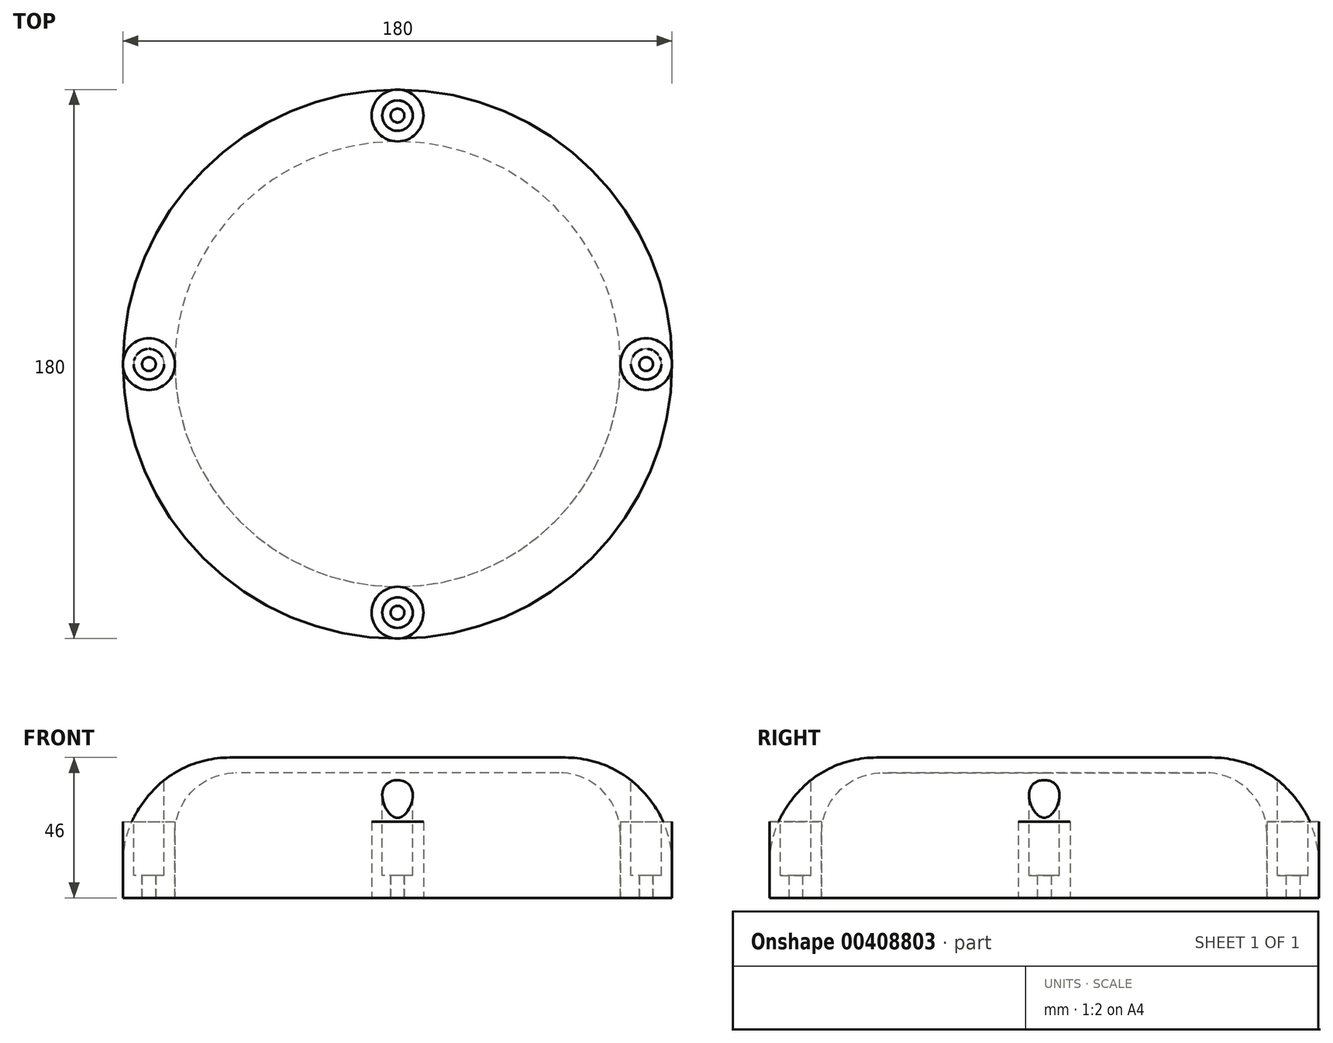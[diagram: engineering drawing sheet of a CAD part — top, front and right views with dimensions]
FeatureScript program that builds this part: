
annotation { "Feature Type Name" : "Feature", "Feature Type Description" : "" }
export const myFeature = defineFeature(function(context is Context, id is Id, definition is map)
    precondition{}
    {
        {
            var Q0;
            Q0=qCreatedBy(makeId("Top.planeOp"),FACE);
            var sketch = newSketch(context, id + "F0", { "sketchPlane" : qUnion([Q0])});
            skCircle(sketch, "E0", {"center": v(0, 0) * mm, "radius": 58 * mm});
            skCircle(sketch, "E1", {"center": v(0, 0) * mm, "radius": 61 * mm});
            skSolve(sketch);
        }
        {
            var Q0;
            Q0=makeQuery(id+"F0.imprint","IMPRINT",FACE,{"disambiguationData":[TD([[makeQuery(id+"F0.imprint","IMPRINT",EDGE,{"derivedFrom":sQuery(id+"F0.wireOp",EDGE,"E0")}),-1.0]])]});
            extrude(context, id + "F1", {"entities" : qUnion([Q0]), "depth" : 4 * mm});
        }
        {
            var Q0;
            Q0=qCreatedBy(makeId("Top.planeOp"),FACE);
            var sketch = newSketch(context, id + "F2", { "sketchPlane" : qUnion([Q0])});
            skCircle(sketch, "E2.0", {"center": v(0, 0) * mm, "radius": 56 * mm});
            skCircle(sketch, "E3.0", {"center": v(0, 0) * mm, "radius": 61 * mm});
            skSolve(sketch);
        }
        {
            var Q0;
            Q0=makeQuery(id+"F2.imprint","IMPRINT",FACE,{"disambiguationData":[TD([[makeQuery(id+"F2.imprint","IMPRINT",EDGE,{"derivedFrom":sQuery(id+"F2.wireOp",EDGE,"E2.0")}),-1.0]])]});
            extrude(context, id + "F3", {"entities" : qUnion([Q0]), "operationType" : NewBodyOperationType.ADD, "oppositeDirection" : true, "depth" : 3 * mm});
        }
        {
            var Q0;
            Q0=makeQuery(id+"F3.opExtrude","CAP_EDGE",EDGE,{"disambiguationData":[OSD([sQuery(id+"F2.wireOp",EDGE,"E2.0")])],"isStart":true});
            chamfer(context, id + "F4", {"entities" : qUnion([Q0]), "width" : 2 * mm, "tangentPropagation" : true});
        }
        {
            var Q0;
            Q0=makeQuery(id+"F3.opExtrude","CAP_FACE",FACE,{"disambiguationData":[OSD([sQuery(id+"F2.wireOp",EDGE,"E2.0"),sQuery(id+"F2.wireOp",EDGE,"E3.0")])],"isStart":false});
            var sketch = newSketch(context, id + "F5", { "sketchPlane" : qUnion([Q0])});
            skCircle(sketch, "E4", {"center": v(-46.45, 46.18) * mm, "radius": 7.5 * mm});
            skLineSegment(sketch, "E5", {"start": v(-53.95, 46.18) * mm, "end": v(-53.95, 28.46) * mm});
            skCircle(sketch, "E6", {"center": v(-46.45, 46.18) * mm, "radius": 2.25 * mm});
            skLineSegment(sketch, "E7", {"start": v(-46.57, 53.68) * mm, "end": v(-28.43, 53.97) * mm});
            skLineSegment(sketch, "E8.1.0", {"start": v(-53.68, -46.57) * mm, "end": v(-53.97, -28.43) * mm});
            skCircle(sketch, "E8.1.1", {"center": v(-46.18, -46.45) * mm, "radius": 7.5 * mm});
            skCircle(sketch, "E8.1.2", {"center": v(-46.18, -46.45) * mm, "radius": 2.25 * mm});
            skLineSegment(sketch, "E8.1.3", {"start": v(-46.18, -53.95) * mm, "end": v(-28.46, -53.95) * mm});
            skLineSegment(sketch, "E8.2.0", {"start": v(46.57, -53.68) * mm, "end": v(28.43, -53.97) * mm});
            skCircle(sketch, "E8.2.1", {"center": v(46.45, -46.18) * mm, "radius": 7.5 * mm});
            skCircle(sketch, "E8.2.2", {"center": v(46.45, -46.18) * mm, "radius": 2.25 * mm});
            skLineSegment(sketch, "E8.2.3", {"start": v(53.95, -46.18) * mm, "end": v(53.95, -28.46) * mm});
            skLineSegment(sketch, "E8.3.0", {"start": v(53.68, 46.57) * mm, "end": v(53.97, 28.43) * mm});
            skCircle(sketch, "E8.3.1", {"center": v(46.18, 46.45) * mm, "radius": 7.5 * mm});
            skCircle(sketch, "E8.3.2", {"center": v(46.18, 46.45) * mm, "radius": 2.25 * mm});
            skLineSegment(sketch, "E8.3.3", {"start": v(46.18, 53.95) * mm, "end": v(28.46, 53.95) * mm});
            skPoint(sketch, "E8.center", {"position": v(0, 0) * mm});
            skSolve(sketch);
        }
        {
            var Q0;
            Q0=qSketchRegion(id+"F5",true);
            var Q1;
            {var subQ0=sQuery(id+"F5.wireOp",EDGE,"E5");Q1=makeQuery(id+"F5.imprint","IMPRINT",FACE,{"disambiguationData":[TD([[makeQuery(id+"F5.imprint","IMPRINT",EDGE,{"derivedFrom":subQ0}),1.0]])]});}
            var Q2;
            {var subQ0=sQuery(id+"F5.wireOp",EDGE,"E7");Q2=makeQuery(id+"F5.imprint","IMPRINT",FACE,{"disambiguationData":[TD([[makeQuery(id+"F5.imprint","IMPRINT",EDGE,{"derivedFrom":subQ0}),-1.0]])]});}
            var Q3;
            {var subQ0=sQuery(id+"F5.wireOp",EDGE,"E8.3.3");Q3=makeQuery(id+"F5.imprint","IMPRINT",FACE,{"disambiguationData":[TD([[makeQuery(id+"F5.imprint","IMPRINT",EDGE,{"derivedFrom":subQ0}),1.0]])]});}
            var Q4;
            {var subQ0=sQuery(id+"F5.wireOp",EDGE,"E8.3.0");Q4=makeQuery(id+"F5.imprint","IMPRINT",FACE,{"disambiguationData":[TD([[makeQuery(id+"F5.imprint","IMPRINT",EDGE,{"derivedFrom":subQ0}),-1.0]])]});}
            var Q5;
            {var subQ0=sQuery(id+"F5.wireOp",EDGE,"E8.2.3");Q5=makeQuery(id+"F5.imprint","IMPRINT",FACE,{"disambiguationData":[TD([[makeQuery(id+"F5.imprint","IMPRINT",EDGE,{"derivedFrom":subQ0}),1.0]])]});}
            var Q6;
            {var subQ0=sQuery(id+"F5.wireOp",EDGE,"E8.2.0");Q6=makeQuery(id+"F5.imprint","IMPRINT",FACE,{"disambiguationData":[TD([[makeQuery(id+"F5.imprint","IMPRINT",EDGE,{"derivedFrom":subQ0}),-1.0]])]});}
            var Q7;
            {var subQ0=sQuery(id+"F5.wireOp",EDGE,"E8.1.3");Q7=makeQuery(id+"F5.imprint","IMPRINT",FACE,{"disambiguationData":[TD([[makeQuery(id+"F5.imprint","IMPRINT",EDGE,{"derivedFrom":subQ0}),1.0]])]});}
            var Q8;
            {var subQ0=sQuery(id+"F5.wireOp",EDGE,"E8.1.0");Q8=makeQuery(id+"F5.imprint","IMPRINT",FACE,{"disambiguationData":[TD([[makeQuery(id+"F5.imprint","IMPRINT",EDGE,{"derivedFrom":subQ0}),-1.0]])]});}
            extrude(context, id + "F6", {"entities" : qUnion([Q0, Q1, Q2, Q3, Q4, Q5, Q6, Q7, Q8]), "operationType" : NewBodyOperationType.ADD, "oppositeDirection" : true, "depth" : 7 * mm});
        }
        {
            var Q0;
            Q0=makeQuery(id+"F6.opExtrude","CAP_EDGE",EDGE,{"disambiguationData":[OSD([sQuery(id+"F5.wireOp",EDGE,"E8.3.2")])],"isStart":true});
            var Q1;
            Q1=makeQuery(id+"F6.opExtrude","CAP_EDGE",EDGE,{"disambiguationData":[OSD([sQuery(id+"F5.wireOp",EDGE,"E8.2.2")])],"isStart":true});
            var Q2;
            Q2=makeQuery(id+"F6.opExtrude","CAP_EDGE",EDGE,{"disambiguationData":[OSD([sQuery(id+"F5.wireOp",EDGE,"E8.1.2")])],"isStart":true});
            var Q3;
            Q3=makeQuery(id+"F6.opExtrude","CAP_EDGE",EDGE,{"disambiguationData":[OSD([sQuery(id+"F5.wireOp",EDGE,"E6")])],"isStart":true});
            chamfer(context, id + "F7", {"entities" : qUnion([Q0, Q1, Q2, Q3]), "width" : 3 * mm, "tangentPropagation" : true});
        }
        {
            var Q0;
            {var subQ0=sQuery(id+"F2.wireOp",EDGE,"E3.0");Q0=makeQuery(id+"F6.boolean.opBoolean","MERGE",FACE,{"derivedFrom":[makeQuery(id+"F1.opExtrude","CAP_FACE",FACE,{"disambiguationData":[OSD([sQuery(id+"F0.wireOp",EDGE,"E0"),sQuery(id+"F0.wireOp",EDGE,"E1")])],"isStart":false}),makeQuery(id+"F6.opExtrude","CAP_FACE",FACE,{"disambiguationData":[OSD([subQ0,sQuery(id+"F5.wireOp",EDGE,"E4"),sQuery(id+"F5.wireOp",EDGE,"E5"),sQuery(id+"F5.wireOp",EDGE,"E6"),sQuery(id+"F5.wireOp",EDGE,"E7")])],"isStart":false}),makeQuery(id+"F6.opExtrude","CAP_FACE",FACE,{"disambiguationData":[OSD([subQ0,sQuery(id+"F5.wireOp",EDGE,"E8.1.0"),sQuery(id+"F5.wireOp",EDGE,"E8.1.1"),sQuery(id+"F5.wireOp",EDGE,"E8.1.2"),sQuery(id+"F5.wireOp",EDGE,"E8.1.3")])],"isStart":false}),makeQuery(id+"F6.opExtrude","CAP_FACE",FACE,{"disambiguationData":[OSD([subQ0,sQuery(id+"F5.wireOp",EDGE,"E8.2.0"),sQuery(id+"F5.wireOp",EDGE,"E8.2.1"),sQuery(id+"F5.wireOp",EDGE,"E8.2.2"),sQuery(id+"F5.wireOp",EDGE,"E8.2.3")])],"isStart":false}),makeQuery(id+"F6.opExtrude","CAP_FACE",FACE,{"disambiguationData":[OSD([subQ0,sQuery(id+"F5.wireOp",EDGE,"E8.3.0"),sQuery(id+"F5.wireOp",EDGE,"E8.3.1"),sQuery(id+"F5.wireOp",EDGE,"E8.3.2"),sQuery(id+"F5.wireOp",EDGE,"E8.3.3")])],"isStart":false})]});}
            var sketch = newSketch(context, id + "F8", { "sketchPlane" : qUnion([Q0])});
            skCircle(sketch, "E9.0", {"center": v(0, 0) * mm, "radius": 56 * mm});
            skCircle(sketch, "E10.0", {"center": v(0, 0) * mm, "radius": 76 * mm});
            skCircle(sketch, "E11", {"center": v(-46.18, 46.45) * mm, "radius": 2.25 * mm});
            skCircle(sketch, "E12", {"center": v(46.45, 46.18) * mm, "radius": 2.25 * mm});
            skCircle(sketch, "E13", {"center": v(46.18, -46.45) * mm, "radius": 2.25 * mm});
            skCircle(sketch, "E14", {"center": v(-46.45, -46.18) * mm, "radius": 2.25 * mm});
            skSolve(sketch);
        }
        {
            var Q0;
            Q0=makeQuery(id+"F8.imprint","IMPRINT",FACE,{"disambiguationData":[TD([[makeQuery(id+"F8.imprint","IMPRINT",EDGE,{"derivedFrom":sQuery(id+"F8.wireOp",EDGE,"E10.0")}),1.0]])]});
            var Q1;
            Q1=makeQuery(id+"F8.imprint","IMPRINT",FACE,{"disambiguationData":[TD([[makeQuery(id+"F8.imprint","IMPRINT",EDGE,{"derivedFrom":sQuery(id+"F8.wireOp",EDGE,"E11")}),1.0]])]});
            extrude(context, id + "F9", {"entities" : qUnion([Q0, Q1]), "operationType" : NewBodyOperationType.ADD, "depth" : 4 * mm});
        }
        {
            var Q0;
            Q0=qCreatedBy(makeId("Right.planeOp"),FACE);
            var sketch = newSketch(context, id + "F10", { "sketchPlane" : qUnion([Q0])});
            skLineSegment(sketch, "E15", {"start": v(89.8, 0) * mm, "end": v(-100.67, 0) * mm});
            skLineSegment(sketch, "E16.0", {"start": v(89.8, 4) * mm, "end": v(-100.67, 4) * mm});
            skLineSegment(sketch, "E17.0", {"start": v(89.8, -3) * mm, "end": v(-100.67, -3) * mm});
            skLineSegment(sketch, "E18", {"start": v(89.8, 4) * mm, "end": v(89.8, -3) * mm});
            skLineSegment(sketch, "E19", {"start": v(-100.67, 4) * mm, "end": v(-100.67, -3) * mm});
            skSolve(sketch);
        }
        {
            var Q0;
            {var subQ0=sQuery(id+"F10.wireOp",EDGE,"E15");Q0=makeQuery(id+"F10.imprint","IMPRINT",FACE,{"disambiguationData":[TD([[makeQuery(id+"F10.imprint","IMPRINT",EDGE,{"derivedFrom":subQ0}),1.0]])]});}
            var Q1;
            {var subQ0=sQuery(id+"F10.wireOp",EDGE,"E15");Q1=makeQuery(id+"F10.imprint","IMPRINT",FACE,{"disambiguationData":[TD([[makeQuery(id+"F10.imprint","IMPRINT",EDGE,{"derivedFrom":subQ0}),-1.0]])]});}
            extrude(context, id + "F11", {"entities" : qUnion([Q0, Q1]), "operationType" : NewBodyOperationType.REMOVE, "endBound" : BoundingType.SYMMETRIC, "depth" : 200 * mm});
        }
        {
            var Q0;
            Q0=makeQuery(id+"F11.boolean.opBoolean","MERGE",FACE,{"derivedFrom":[makeQuery(id+"F9.opExtrude","CAP_FACE",FACE,{"disambiguationData":[OSD([sQuery(id+"F0.wireOp",EDGE,"E0"),sQuery(id+"F8.wireOp",EDGE,"E10.0"),sQuery(id+"F8.wireOp",EDGE,"E11"),sQuery(id+"F8.wireOp",EDGE,"E12"),sQuery(id+"F8.wireOp",EDGE,"E13"),sQuery(id+"F8.wireOp",EDGE,"E14")])],"isStart":true}),makeQuery(id+"F11.opExtrude","SWEPT_FACE",FACE,{"disambiguationData":[OSD([sQuery(id+"F10.wireOp",EDGE,"E16.0")])]})]});
            var sketch = newSketch(context, id + "F12", { "sketchPlane" : qUnion([Q0])});
            skCircle(sketch, "E20.0", {"center": v(0, 0) * mm, "radius": 73 * mm});
            skCircle(sketch, "E21.0", {"center": v(0, 0) * mm, "radius": 90 * mm});
            skCircle(sketch, "E22", {"center": v(0, 81.5) * mm, "radius": 8.5 * mm});
            skCircle(sketch, "E23", {"center": v(0, 81.5) * mm, "radius": 2.25 * mm});
            skCircle(sketch, "E24.1.0", {"center": v(-81.5, 0) * mm, "radius": 2.25 * mm});
            skCircle(sketch, "E24.1.1", {"center": v(-81.5, 0) * mm, "radius": 8.5 * mm});
            skCircle(sketch, "E24.2.0", {"center": v(0, -81.5) * mm, "radius": 2.25 * mm});
            skCircle(sketch, "E24.2.1", {"center": v(0, -81.5) * mm, "radius": 8.5 * mm});
            skCircle(sketch, "E24.3.0", {"center": v(81.5, 0) * mm, "radius": 2.25 * mm});
            skCircle(sketch, "E24.3.1", {"center": v(81.5, 0) * mm, "radius": 8.5 * mm});
            skSolve(sketch);
        }
        {
            var Q0;
            Q0 = qSketchRegion(id + "F12", true);
            var Q1;
            Q1 = qSketchRegion(id + "F14", true);
            extrude(context, id + "F13", {"entities" : qUnion([Q0, Q1]), "operationType" : NewBodyOperationType.ADD, "depth" : 50 * mm});
        }
        {
            var Q0;
            Q0=makeQuery(id+"F13.opExtrude","CAP_FACE",FACE,{"disambiguationData":[OSD([sQuery(id+"F12.wireOp",EDGE,"E20.0"),sQuery(id+"F12.wireOp",EDGE,"E21.0"),sQuery(id+"F12.wireOp",EDGE,"E23"),sQuery(id+"F12.wireOp",EDGE,"E24.1.0"),sQuery(id+"F12.wireOp",EDGE,"E24.2.0"),sQuery(id+"F12.wireOp",EDGE,"E24.3.0")])],"isStart":false});
            var sketch = newSketch(context, id + "F14", { "sketchPlane" : qUnion([Q0])});
            skCircle(sketch, "E25", {"center": v(-81.5, 0) * mm, "radius": 8.5 * mm});
            skCircle(sketch, "E26.1.0", {"center": v(0, -81.5) * mm, "radius": 8.5 * mm});
            skCircle(sketch, "E26.2.0", {"center": v(81.5, 0) * mm, "radius": 8.5 * mm});
            skCircle(sketch, "E26.3.0", {"center": v(0, 81.5) * mm, "radius": 8.5 * mm});
            skPoint(sketch, "E26.center", {"position": v(0, 0) * mm});
            skSolve(sketch);
        }
        {
            var Q0;
            {var subQ0=sQuery(id+"F14.wireOp",EDGE,"E25");var subQ1=sQuery(id+"F12.wireOp",EDGE,"E20.0");var subQ2=makeQuery(id+"F0B67d8czmStKe8_1.opChamfer","BLEND_EDGE",EDGE,{"blendedFrom":[makeQuery(id+"F13.opExtrude","CAP_EDGE",EDGE,{"disambiguationData":[OSD([subQ1])],"isStart":false}),makeQuery(id+"F13.opExtrude","CAP_FACE",FACE,{"disambiguationData":[OSD([subQ1,sQuery(id+"F12.wireOp",EDGE,"E21.0"),sQuery(id+"F12.wireOp",EDGE,"E23"),sQuery(id+"F12.wireOp",EDGE,"E24.1.0"),sQuery(id+"F12.wireOp",EDGE,"E24.2.0"),sQuery(id+"F12.wireOp",EDGE,"E24.3.0")])],"isStart":false})],"blendedInto":[makeQuery(id+"F13.opExtrude","CAP_FACE",FACE,{"disambiguationData":[OSD([subQ1,sQuery(id+"F12.wireOp",EDGE,"E21.0"),sQuery(id+"F12.wireOp",EDGE,"E23"),sQuery(id+"F12.wireOp",EDGE,"E24.1.0"),sQuery(id+"F12.wireOp",EDGE,"E24.2.0"),sQuery(id+"F12.wireOp",EDGE,"E24.3.0")])],"isStart":false})]});var subQ3=makeQuery(id+"F14.imprint","INTERSECT",VERTEX,{"disambiguationData":[OD(0.0)],"derivedFrom":[subQ2,subQ0]});Q0=makeQuery(id+"F14.imprint","IMPRINT",FACE,{"disambiguationData":[TD([[makeQuery(id+"F14.imprint","IMPRINT",EDGE,{"disambiguationData":[TD([[subQ3,1.0]])],"derivedFrom":subQ0}),1.0]])]});}
            var Q1;
            {var subQ0=sQuery(id+"F14.wireOp",EDGE,"E26.3.0");var subQ1=sQuery(id+"F12.wireOp",EDGE,"E20.0");var subQ2=makeQuery(id+"F0B67d8czmStKe8_1.opChamfer","BLEND_EDGE",EDGE,{"blendedFrom":[makeQuery(id+"F13.opExtrude","CAP_EDGE",EDGE,{"disambiguationData":[OSD([subQ1])],"isStart":false}),makeQuery(id+"F13.opExtrude","CAP_FACE",FACE,{"disambiguationData":[OSD([subQ1,sQuery(id+"F12.wireOp",EDGE,"E21.0"),sQuery(id+"F12.wireOp",EDGE,"E23"),sQuery(id+"F12.wireOp",EDGE,"E24.1.0"),sQuery(id+"F12.wireOp",EDGE,"E24.2.0"),sQuery(id+"F12.wireOp",EDGE,"E24.3.0")])],"isStart":false})],"blendedInto":[makeQuery(id+"F13.opExtrude","CAP_FACE",FACE,{"disambiguationData":[OSD([subQ1,sQuery(id+"F12.wireOp",EDGE,"E21.0"),sQuery(id+"F12.wireOp",EDGE,"E23"),sQuery(id+"F12.wireOp",EDGE,"E24.1.0"),sQuery(id+"F12.wireOp",EDGE,"E24.2.0"),sQuery(id+"F12.wireOp",EDGE,"E24.3.0")])],"isStart":false})]});var subQ3=makeQuery(id+"F14.imprint","INTERSECT",VERTEX,{"disambiguationData":[OD(0.0)],"derivedFrom":[subQ2,subQ0]});Q1=makeQuery(id+"F14.imprint","IMPRINT",FACE,{"disambiguationData":[TD([[makeQuery(id+"F14.imprint","IMPRINT",EDGE,{"disambiguationData":[TD([[subQ3,1.0]])],"derivedFrom":subQ0}),1.0]])]});}
            var Q2;
            {var subQ0=sQuery(id+"F14.wireOp",EDGE,"E26.2.0");var subQ1=sQuery(id+"F12.wireOp",EDGE,"E20.0");var subQ2=makeQuery(id+"F0B67d8czmStKe8_1.opChamfer","BLEND_EDGE",EDGE,{"blendedFrom":[makeQuery(id+"F13.opExtrude","CAP_EDGE",EDGE,{"disambiguationData":[OSD([subQ1])],"isStart":false}),makeQuery(id+"F13.opExtrude","CAP_FACE",FACE,{"disambiguationData":[OSD([subQ1,sQuery(id+"F12.wireOp",EDGE,"E21.0"),sQuery(id+"F12.wireOp",EDGE,"E23"),sQuery(id+"F12.wireOp",EDGE,"E24.1.0"),sQuery(id+"F12.wireOp",EDGE,"E24.2.0"),sQuery(id+"F12.wireOp",EDGE,"E24.3.0")])],"isStart":false})],"blendedInto":[makeQuery(id+"F13.opExtrude","CAP_FACE",FACE,{"disambiguationData":[OSD([subQ1,sQuery(id+"F12.wireOp",EDGE,"E21.0"),sQuery(id+"F12.wireOp",EDGE,"E23"),sQuery(id+"F12.wireOp",EDGE,"E24.1.0"),sQuery(id+"F12.wireOp",EDGE,"E24.2.0"),sQuery(id+"F12.wireOp",EDGE,"E24.3.0")])],"isStart":false})]});var subQ3=makeQuery(id+"F14.imprint","INTERSECT",VERTEX,{"disambiguationData":[OD(0.0)],"derivedFrom":[subQ2,subQ0]});Q2=makeQuery(id+"F14.imprint","IMPRINT",FACE,{"disambiguationData":[TD([[makeQuery(id+"F14.imprint","IMPRINT",EDGE,{"disambiguationData":[TD([[subQ3,1.0]])],"derivedFrom":subQ0}),1.0]])]});}
            var Q3;
            {var subQ0=sQuery(id+"F14.wireOp",EDGE,"E26.1.0");var subQ1=sQuery(id+"F12.wireOp",EDGE,"E20.0");var subQ2=makeQuery(id+"F0B67d8czmStKe8_1.opChamfer","BLEND_EDGE",EDGE,{"blendedFrom":[makeQuery(id+"F13.opExtrude","CAP_EDGE",EDGE,{"disambiguationData":[OSD([subQ1])],"isStart":false}),makeQuery(id+"F13.opExtrude","CAP_FACE",FACE,{"disambiguationData":[OSD([subQ1,sQuery(id+"F12.wireOp",EDGE,"E21.0"),sQuery(id+"F12.wireOp",EDGE,"E23"),sQuery(id+"F12.wireOp",EDGE,"E24.1.0"),sQuery(id+"F12.wireOp",EDGE,"E24.2.0"),sQuery(id+"F12.wireOp",EDGE,"E24.3.0")])],"isStart":false})],"blendedInto":[makeQuery(id+"F13.opExtrude","CAP_FACE",FACE,{"disambiguationData":[OSD([subQ1,sQuery(id+"F12.wireOp",EDGE,"E21.0"),sQuery(id+"F12.wireOp",EDGE,"E23"),sQuery(id+"F12.wireOp",EDGE,"E24.1.0"),sQuery(id+"F12.wireOp",EDGE,"E24.2.0"),sQuery(id+"F12.wireOp",EDGE,"E24.3.0")])],"isStart":false})]});var subQ3=makeQuery(id+"F14.imprint","INTERSECT",VERTEX,{"disambiguationData":[OD(0.0)],"derivedFrom":[subQ2,subQ0]});Q3=makeQuery(id+"F14.imprint","IMPRINT",FACE,{"disambiguationData":[TD([[makeQuery(id+"F14.imprint","IMPRINT",EDGE,{"disambiguationData":[TD([[subQ3,1.0]])],"derivedFrom":subQ0}),1.0]])]});}
            extrude(context, id + "F15", {"entities" : qUnion([Q0, Q1, Q2, Q3]), "oppositeDirection" : true, "depth" : 25 * mm});
        }
        {
            var Q0;
            Q0=makeQuery(id+"F12.imprint","IMPRINT",FACE,{"disambiguationData":[TD([[makeQuery(id+"F12.imprint","IMPRINT",EDGE,{"derivedFrom":sQuery(id+"F12.wireOp",EDGE,"E24.1.0")}),1.0]])]});
            var Q1;
            Q1=makeQuery(id+"F12.imprint","IMPRINT",FACE,{"disambiguationData":[TD([[makeQuery(id+"F12.imprint","IMPRINT",EDGE,{"derivedFrom":sQuery(id+"F12.wireOp",EDGE,"E24.2.0")}),1.0]])]});
            var Q2;
            Q2=makeQuery(id+"F12.imprint","IMPRINT",FACE,{"disambiguationData":[TD([[makeQuery(id+"F12.imprint","IMPRINT",EDGE,{"derivedFrom":sQuery(id+"F12.wireOp",EDGE,"E24.3.0")}),1.0]])]});
            var Q3;
            Q3=makeQuery(id+"F12.imprint","IMPRINT",FACE,{"disambiguationData":[TD([[makeQuery(id+"F12.imprint","IMPRINT",EDGE,{"derivedFrom":sQuery(id+"F12.wireOp",EDGE,"E23")}),1.0]])]});
            extrude(context, id + "F16", {"entities" : qUnion([Q0, Q1, Q2, Q3]), "operationType" : NewBodyOperationType.REMOVE, "depth" : 73 * mm});
        }
        {
            var Q0;
            Q0=makeQuery(id+"F9.opExtrude","CAP_FACE",FACE,{"disambiguationData":[OSD([sQuery(id+"F0.wireOp",EDGE,"E0"),sQuery(id+"F8.wireOp",EDGE,"E10.0"),sQuery(id+"F8.wireOp",EDGE,"E11"),sQuery(id+"F8.wireOp",EDGE,"E12"),sQuery(id+"F8.wireOp",EDGE,"E13"),sQuery(id+"F8.wireOp",EDGE,"E14")])],"isStart":false});
            var sketch = newSketch(context, id + "F17", { "sketchPlane" : qUnion([Q0])});
            skCircle(sketch, "E27", {"center": v(0, 81.5) * mm, "radius": 5 * mm});
            skCircle(sketch, "E28.1.0", {"center": v(-81.5, 0) * mm, "radius": 5 * mm});
            skCircle(sketch, "E28.2.0", {"center": v(0, -81.5) * mm, "radius": 5 * mm});
            skCircle(sketch, "E28.3.0", {"center": v(81.5, 0) * mm, "radius": 5 * mm});
            skPoint(sketch, "E28.center", {"position": v(0, 0) * mm});
            skSolve(sketch);
        }
        {
            var Q0;
            Q0=makeQuery(id+"F17.imprint","IMPRINT",FACE,{"disambiguationData":[TD([[makeQuery(id+"F17.imprint","IMPRINT",EDGE,{"derivedFrom":sQuery(id+"F17.wireOp",EDGE,"E27")}),1.0]])]});
            var Q1;
            Q1=makeQuery(id+"F17.imprint","IMPRINT",FACE,{"disambiguationData":[TD([[makeQuery(id+"F17.imprint","IMPRINT",EDGE,{"derivedFrom":sQuery(id+"F17.wireOp",EDGE,"E28.1.0")}),1.0]])]});
            var Q2;
            Q2=makeQuery(id+"F17.imprint","IMPRINT",FACE,{"disambiguationData":[TD([[makeQuery(id+"F17.imprint","IMPRINT",EDGE,{"derivedFrom":sQuery(id+"F17.wireOp",EDGE,"E28.3.0")}),1.0]])]});
            var Q3;
            Q3=makeQuery(id+"F17.imprint","IMPRINT",FACE,{"disambiguationData":[TD([[makeQuery(id+"F17.imprint","IMPRINT",EDGE,{"derivedFrom":sQuery(id+"F17.wireOp",EDGE,"E28.2.0")}),1.0]])]});
            extrude(context, id + "F18", {"entities" : qUnion([Q0, Q1, Q2, Q3]), "operationType" : NewBodyOperationType.REMOVE, "oppositeDirection" : true, "depth" : 46.7 * mm});
        }
        {
            var Q0;
            Q0=qCreatedBy(makeId("Right.planeOp"),FACE);
            var sketch = newSketch(context, id + "F19", { "sketchPlane" : qUnion([Q0])});
            skLineSegment(sketch, "E29", {"start": v(-101.83, 0) * mm, "end": v(102.03, 0) * mm});
            skLineSegment(sketch, "E30", {"start": v(102.03, 0) * mm, "end": v(102.03, 25.22) * mm});
            skLineSegment(sketch, "E31", {"start": v(102.03, 25.22) * mm, "end": v(-100.47, 25.22) * mm});
            skLineSegment(sketch, "E32", {"start": v(-100.47, 25.22) * mm, "end": v(-101.83, 0) * mm});
            skSolve(sketch);
        }
        {
            var Q0;
            Q0=makeQuery(id+"F19.imprint","IMPRINT",FACE,{"disambiguationData":[TD([[makeQuery(id+"F19.imprint","IMPRINT",EDGE,{"derivedFrom":sQuery(id+"F19.wireOp",EDGE,"E29")}),1.0]])]});
            extrude(context, id + "F20", {"entities" : qUnion([Q0]), "operationType" : NewBodyOperationType.REMOVE, "endBound" : BoundingType.SYMMETRIC, "depth" : 800 * mm});
        }
        {
            var Q0;
            Q0=makeQuery(id+"F20.boolean.opBoolean","COPY",FACE,{"derivedFrom":makeQuery(id+"F20.opExtrude","SWEPT_FACE",FACE,{"disambiguationData":[OSD([sQuery(id+"F19.wireOp",EDGE,"E29")])]})});
            var sketch = newSketch(context, id + "F21", { "sketchPlane" : qUnion([Q0])});
            skCircle(sketch, "E33", {"center": v(0, 0) * mm, "radius": 73.5 * mm});
            skSolve(sketch);
        }
        {
            var Q0;
            Q0 = qSketchRegion(id + "F21", true);
            extrude(context, id + "F22", {"entities" : qUnion([Q0]), "operationType" : NewBodyOperationType.ADD, "oppositeDirection" : true, "depth" : 5 * mm});
        }
        {
            var Q0;
            Q0=makeQuery(id+"F20.boolean.opBoolean","INTERSECT",EDGE,{"derivedFrom":[makeQuery(id+"F13.opExtrude","SWEPT_FACE",FACE,{"disambiguationData":[OSD([sQuery(id+"F12.wireOp",EDGE,"E21.0")])]}),makeQuery(id+"F20.opExtrude","SWEPT_FACE",FACE,{"disambiguationData":[OSD([sQuery(id+"F19.wireOp",EDGE,"E29")])]})]});
            fillet(context, id + "F23", {"entities" : qUnion([Q0]), "radius" : 35 * mm, "tangentPropagation" : true, "allowEdgeOverflow" : false});
        }
        {
            var Q0;
            Q0=makeQuery(id+"F22.boolean.opBoolean","INTERSECT",EDGE,{"derivedFrom":[makeQuery(id+"F13.opExtrude","SWEPT_FACE",FACE,{"disambiguationData":[OSD([sQuery(id+"F12.wireOp",EDGE,"E20.0")])]}),makeQuery(id+"F22.opExtrude","CAP_FACE",FACE,{"disambiguationData":[OSD([sQuery(id+"F21.wireOp",EDGE,"E33")])],"isStart":false})]});
            fillet(context, id + "F24", {"entities" : qUnion([Q0]), "radius" : 20 * mm, "tangentPropagation" : true, "allowEdgeOverflow" : false});
        }
    });
